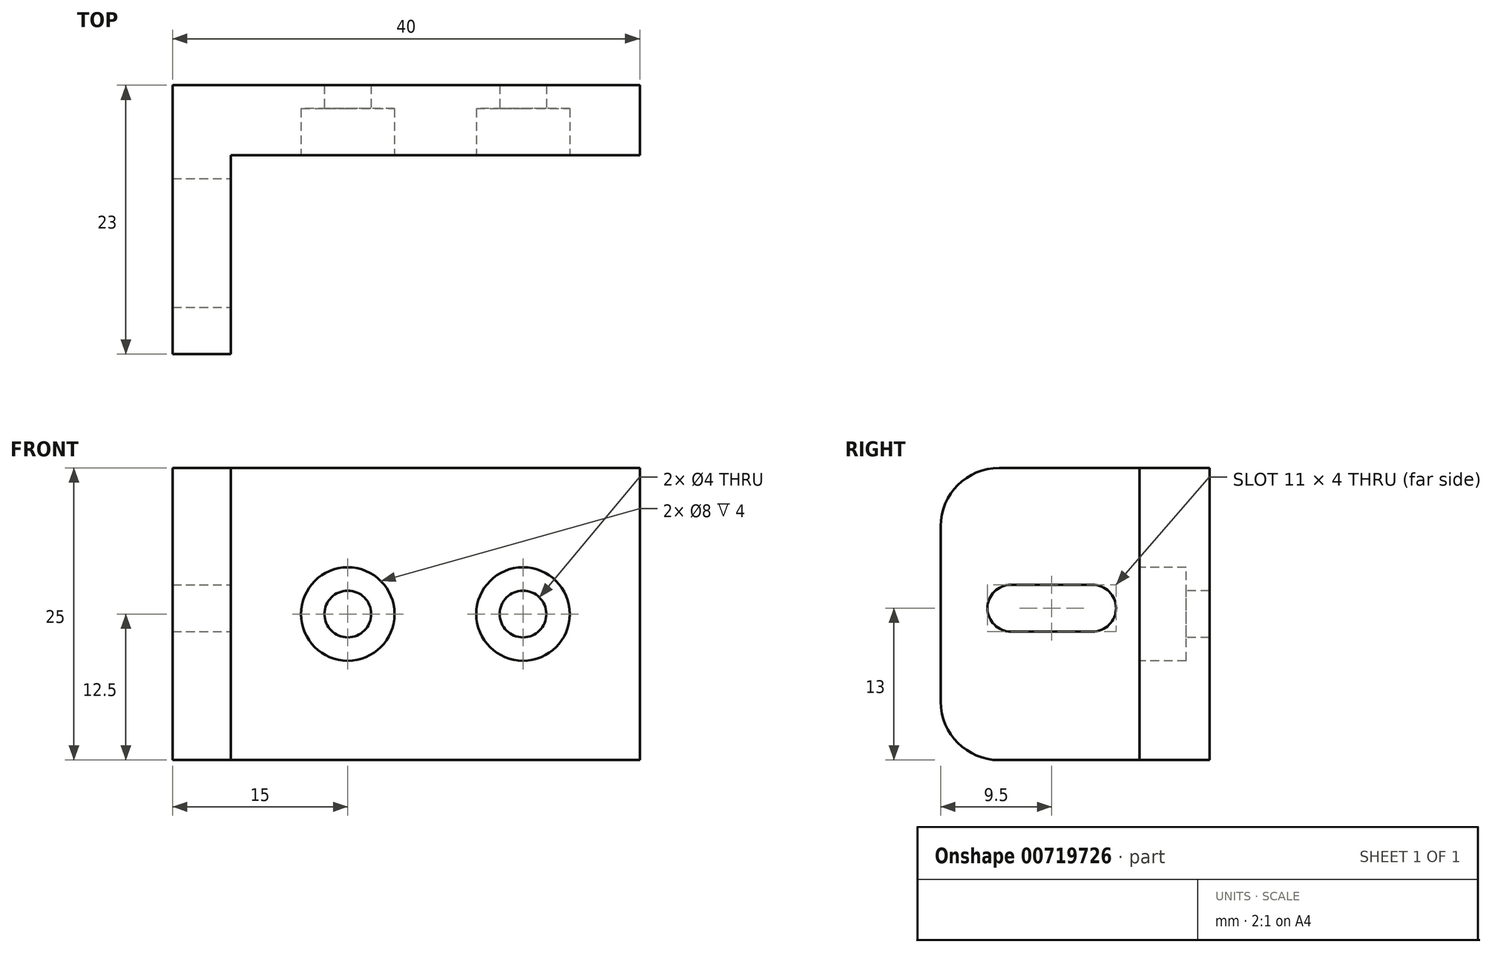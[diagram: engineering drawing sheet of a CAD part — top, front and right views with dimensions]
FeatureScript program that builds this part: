
annotation { "Feature Type Name" : "Feature", "Feature Type Description" : "" }
export const myFeature = defineFeature(function(context is Context, id is Id, definition is map)
    precondition{}
    {
        {
            var Q0;
            Q0=qCreatedBy(makeId("Top.planeOp"),FACE);
            var sketch = newSketch(context, id + "F0", { "sketchPlane" : qUnion([Q0])});
            skLineSegment(sketch, "E0", {"start": v(0, -23) * mm, "end": v(0, 0) * mm});
            skLineSegment(sketch, "E1", {"start": v(0, 0) * mm, "end": v(40, 0) * mm});
            skLineSegment(sketch, "E2", {"start": v(40, 0) * mm, "end": v(40, -6) * mm});
            skLineSegment(sketch, "E3", {"start": v(5, -6) * mm, "end": v(5, -23) * mm});
            skLineSegment(sketch, "E4", {"start": v(5, -23) * mm, "end": v(0, -23) * mm});
            skLineSegment(sketch, "E5", {"start": v(5, -6) * mm, "end": v(40, -6) * mm});
            skSolve(sketch);
        }
        {
            var Q0;
            Q0 = qSketchRegion(id + "F0", true);
            var Q1;
            Q1=makeQuery(id+"F0.imprint","IMPRINT",FACE,{"disambiguationData":[TD([[makeQuery(id+"F0.imprint","IMPRINT",EDGE,{"derivedFrom":sQuery(id+"F0.wireOp",EDGE,"CrukEB1T-zeXr-Sad0-vFso-s5Saf3FCMIQa")}),-1.0]])]});
            extrude(context, id + "F1", {"entities" : qUnion([Q0, Q1]), "depth" : 25 * mm, "offsetDistance" : 25 * mm});
        }
        {
            var Q0;
            Q0=makeQuery(id+"F1.opExtrude","CAP_EDGE",EDGE,{"disambiguationData":[OSD([sQuery(id+"F0.wireOp",EDGE,"E4")])],"isStart":true});
            var Q1;
            Q1=makeQuery(id+"F1.opExtrude","CAP_EDGE",EDGE,{"disambiguationData":[OSD([sQuery(id+"F0.wireOp",EDGE,"E4")])],"isStart":false});
            fillet(context, id + "F2", {"entities" : qUnion([Q0, Q1]), "radius" : 5 * mm, "tangentPropagation" : true, "allowEdgeOverflow" : false});
        }
        {
            var Q0;
            Q0=makeQuery(id+"F1.opExtrude","SWEPT_FACE",FACE,{"disambiguationData":[OSD([sQuery(id+"F0.wireOp",EDGE,"E3")])]});
            var sketch = newSketch(context, id + "F3", { "sketchPlane" : qUnion([Q0])});
            skLineSegment(sketch, "E6.bottom", {"start": v(-17, 11) * mm, "end": v(-10, 11) * mm});
            skLineSegment(sketch, "E6.top", {"start": v(-17, 15) * mm, "end": v(-10, 15) * mm});
            skLineSegment(sketch, "E6.left", {"start": v(-17, 11) * mm, "end": v(-17, 11) * mm});
            skArc(sketch, "E7", {"start": v(-17, 15) * mm, "mid": v(-19, 13) * mm, "end": v(-17, 11) * mm});
            skArc(sketch, "E8", {"start": v(-10, 11) * mm, "mid": v(-8, 13) * mm, "end": v(-10, 15) * mm});
            skLineSegment(sketch, "E9.trimOffspring", {"start": v(-17, 15) * mm, "end": v(-17, 15) * mm});
            skSolve(sketch);
        }
        {
            var Q0;
            Q0 = qSketchRegion(id + "F3", true);
            extrude(context, id + "F4", {"entities" : qUnion([Q0]), "operationType" : NewBodyOperationType.REMOVE, "endBound" : BoundingType.THROUGH_ALL, "oppositeDirection" : true, "depth" : 25 * mm, "offsetDistance" : 25 * mm});
        }
        {
            var Q0;
            Q0=makeQuery(id+"F1.opExtrude","SWEPT_FACE",FACE,{"disambiguationData":[OSD([sQuery(id+"F0.wireOp",EDGE,"E5")])]});
            var sketch = newSketch(context, id + "F5", { "sketchPlane" : qUnion([Q0])});
            skCircle(sketch, "E10", {"center": v(30, 12.5) * mm, "radius": 1.5 * mm});
            skCircle(sketch, "E11", {"center": v(15, 12.5) * mm, "radius": 1.5 * mm});
            skSolve(sketch);
        }
        {
            var Q0;
            Q0=sQuery(id+"F5.wireOp",VERTEX,"E10.center");
            var Q1;
            Q1=sQuery(id+"F5.wireOp",VERTEX,"E11.center");
            var Q2;
            Q2=makeQuery(id+"F1.opExtrude","SWEPT_BODY",BODY,{"disambiguationData":[OSD([sQuery(id+"F0.wireOp",EDGE,"E0"),sQuery(id+"F0.wireOp",EDGE,"E1"),sQuery(id+"F0.wireOp",EDGE,"E2"),sQuery(id+"F0.wireOp",EDGE,"E3"),sQuery(id+"F0.wireOp",EDGE,"E4"),sQuery(id+"F0.wireOp",EDGE,"E5")])]});
            hole(context, id + "F6", {"style" : HoleStyle.C_BORE, "endStyle" : HoleEndStyle.THROUGH, "holeDiameter" : 4 * mm, "cBoreDiameter" : 8 * mm, "cBoreDepth" : 4 * mm, "majorDiameter" : 5 * mm, "isTappedThrough" : true, "tappedDepth" : 12 * mm, "tapClearance" : 3, "locations" : qUnion([Q0, Q1]), "scope" : qUnion([Q2])});
        }
    });
